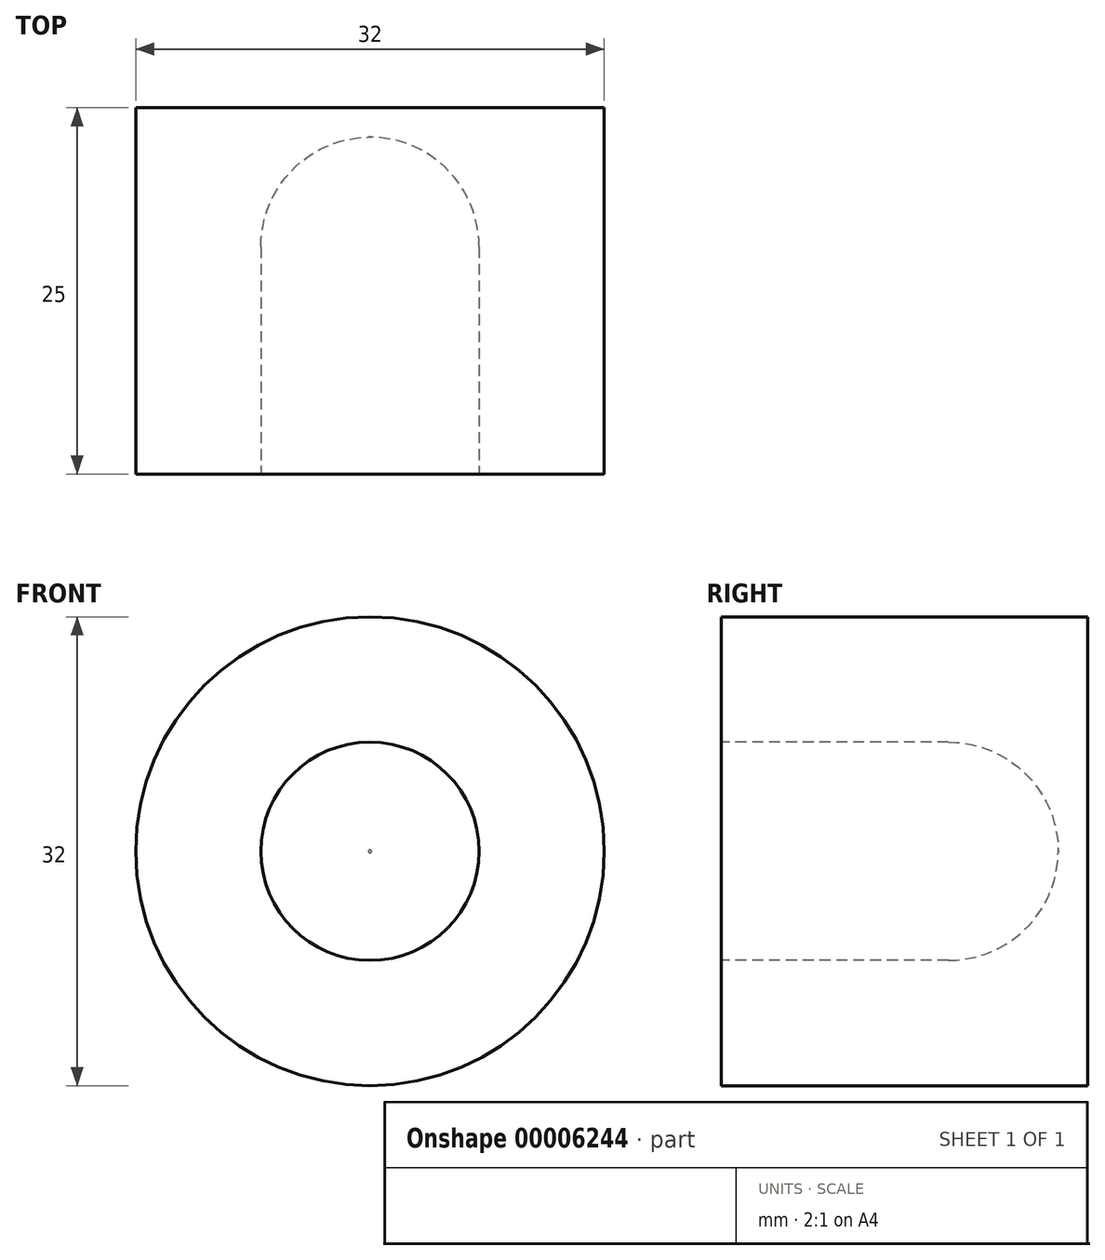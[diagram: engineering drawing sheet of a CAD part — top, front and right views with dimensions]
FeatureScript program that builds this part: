
annotation { "Feature Type Name" : "Feature", "Feature Type Description" : "" }
export const myFeature = defineFeature(function(context is Context, id is Id, definition is map)
    precondition{}
    {
        {
            var Q0;
            Q0=qCreatedBy(makeId("Right.planeOp"),FACE);
            var sketch = newSketch(context, id + "F0", { "sketchPlane" : qUnion([Q0])});
            skLineSegment(sketch, "E0.bottom", {"start": v(0, 0) * mm, "end": v(25, 0) * mm});
            skLineSegment(sketch, "E0.top", {"start": v(0, 16) * mm, "end": v(25, 16) * mm});
            skLineSegment(sketch, "E0.left", {"start": v(0, 0) * mm, "end": v(0, 16) * mm});
            skLineSegment(sketch, "E0.right", {"start": v(25, 0) * mm, "end": v(25, 16) * mm});
            skLineSegment(sketch, "E1", {"start": v(0, 7.45) * mm, "end": v(15.5, 7.45) * mm});
            skArc(sketch, "E2", {"start": v(15.5, 7.45) * mm, "mid": v(20.79, 5.27) * mm, "end": v(23, 0) * mm});
            skSolve(sketch);
        }
        {
            var Q0;
            {var subQ3=sQuery(id+"F0.wireOp",EDGE,"E0.top");Q0=makeQuery(id+"F0.imprint","IMPRINT",FACE,{"disambiguationData":[TD([[makeQuery(id+"F0.imprint","IMPRINT",EDGE,{"derivedFrom":subQ3}),-1.0]])]});}
            var Q1;
            Q1=sQuery(id+"F0.wireOp",EDGE,"E0.bottom");
            revolve(context, id + "F1", {"entities" : qUnion([Q0]), "axis" : qUnion([Q1]), "revolveType" : RevolveType.FULL});
        }
    });
